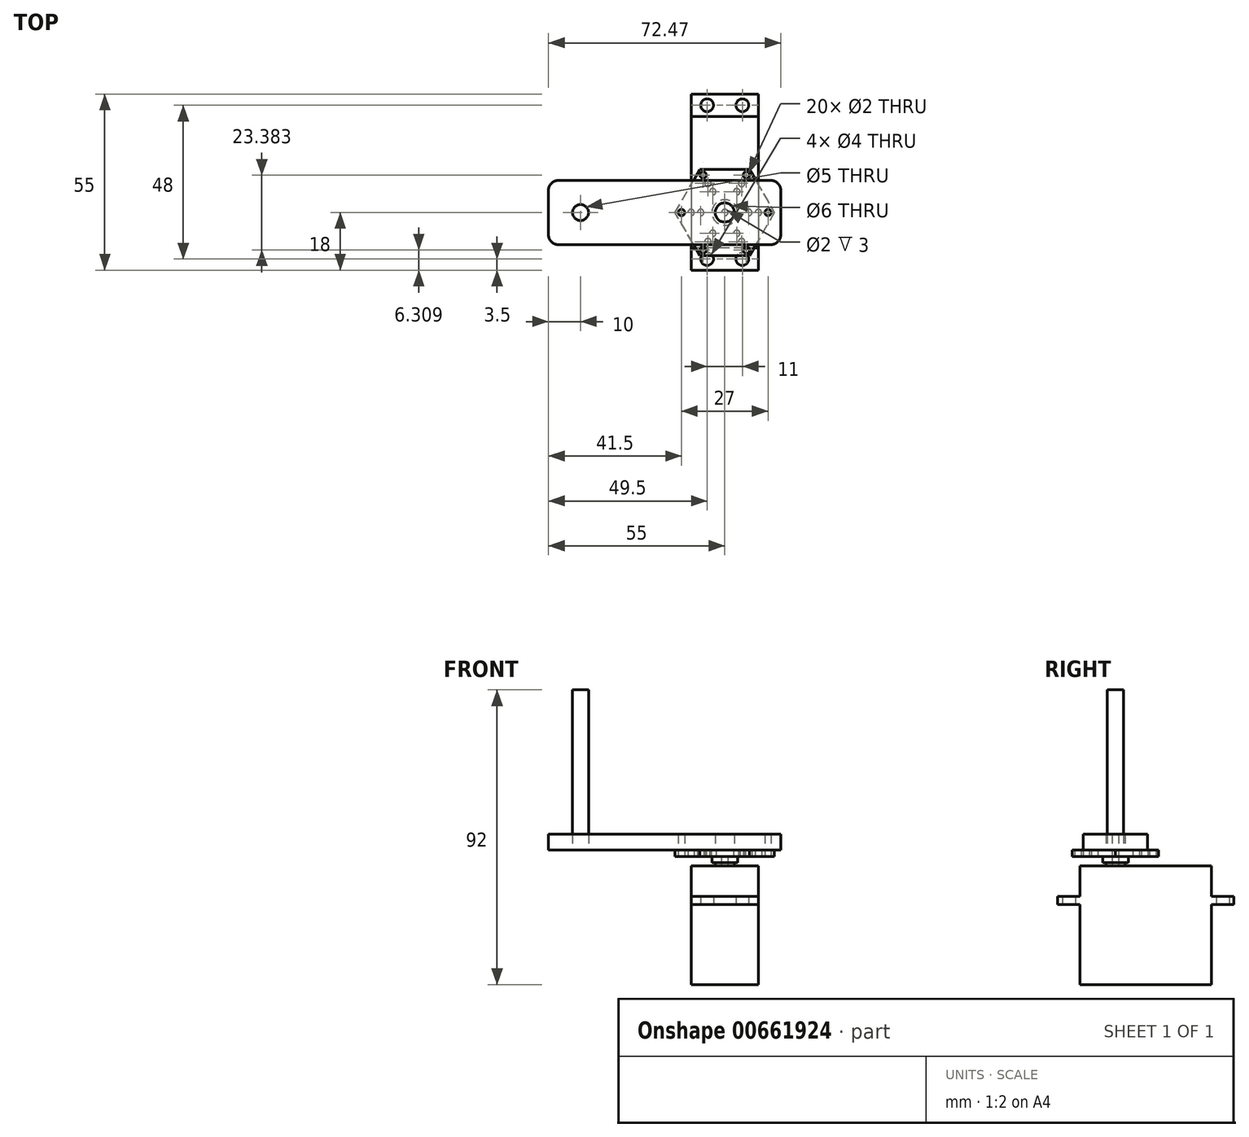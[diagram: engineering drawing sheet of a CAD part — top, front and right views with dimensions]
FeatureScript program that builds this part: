
annotation { "Feature Type Name" : "Feature", "Feature Type Description" : "" }
export const myFeature = defineFeature(function(context is Context, id is Id, definition is map)
    precondition{}
    {
        {
            var Q0;
            Q0=qCreatedBy(makeId("Top.planeOp"),FACE);
            var sketch = newSketch(context, id + "F0", { "sketchPlane" : qUnion([Q0])});
            skLineSegment(sketch, "E0.bottom", {"start": v(10.5, 20.5) * mm, "end": v(-10.5, 20.5) * mm});
            skLineSegment(sketch, "E0.top", {"start": v(10.5, -20.5) * mm, "end": v(-10.5, -20.5) * mm});
            skLineSegment(sketch, "E0.left", {"start": v(10.5, 20.5) * mm, "end": v(10.5, -20.5) * mm});
            skLineSegment(sketch, "E0.right", {"start": v(-10.5, 20.5) * mm, "end": v(-10.5, -20.5) * mm});
            skPoint(sketch, "E0.middle", {"position": v(0, 0) * mm});
            skSolve(sketch);
        }
        {
            var Q0;
            Q0 = qSketchRegion(id + "F0", true);
            extrude(context, id + "F1", {"entities" : qUnion([Q0]), "depth" : 12 * mm, "offsetDistance" : 25 * mm, "hasSecondDirection" : true, "secondDirectionOppositeDirection" : true, "secondDirectionDepth" : 25 * mm});
        }
        {
            var Q0;
            Q0=qCreatedBy(makeId("Top.planeOp"),FACE);
            var sketch = newSketch(context, id + "F2", { "sketchPlane" : qUnion([Q0])});
            skLineSegment(sketch, "E1.bottom", {"start": v(10.5, 27.5) * mm, "end": v(-10.5, 27.5) * mm});
            skLineSegment(sketch, "E1.top", {"start": v(10.5, -27.5) * mm, "end": v(-10.5, -27.5) * mm});
            skLineSegment(sketch, "E1.left", {"start": v(10.5, 27.5) * mm, "end": v(10.5, -27.5) * mm});
            skLineSegment(sketch, "E1.right", {"start": v(-10.5, 27.5) * mm, "end": v(-10.5, -27.5) * mm});
            skPoint(sketch, "E1.middle", {"position": v(0, 0) * mm});
            skLineSegment(sketch, "E2", {"start": v(0, 32.48) * mm, "end": v(0, -40.95) * mm, "construction": true});
            skPoint(sketch, "E2.endSnap0", {"position": v(0, -27.5) * mm});
            skCircle(sketch, "E3", {"center": v(-5.5, 24) * mm, "radius": 2 * mm});
            skLineSegment(sketch, "E4", {"start": v(-14.54, 0) * mm, "end": v(15.38, 0) * mm, "construction": true});
            skCircle(sketch, "E5.MirrorC", {"center": v(5.5, 24) * mm, "radius": 2 * mm});
            skCircle(sketch, "E6.MirrorC", {"center": v(5.5, -24) * mm, "radius": 2 * mm});
            skCircle(sketch, "E7.MirrorC", {"center": v(-5.5, -24) * mm, "radius": 2 * mm});
            skSolve(sketch);
        }
        {
            var Q0;
            Q0 = qSketchRegion(id + "F2", true);
            extrude(context, id + "F3", {"entities" : qUnion([Q0]), "operationType" : NewBodyOperationType.ADD, "depth" : 2.5 * mm, "offsetDistance" : 25 * mm});
        }
        {
            var Q0;
            Q0=makeQuery(id+"F1.opExtrude","CAP_FACE",FACE,{"disambiguationData":[OSD([sQuery(id+"F0.wireOp",EDGE,"E0.bottom"),sQuery(id+"F0.wireOp",EDGE,"E0.top"),sQuery(id+"F0.wireOp",EDGE,"E0.left"),sQuery(id+"F0.wireOp",EDGE,"E0.right")])],"isStart":false});
            var sketch = newSketch(context, id + "F4", { "sketchPlane" : qUnion([Q0])});
            skCircle(sketch, "E8", {"center": v(0, -9.5) * mm, "radius": 3 * mm});
            skCircle(sketch, "E9", {"center": v(0, -9.5) * mm, "radius": 1 * mm});
            skSolve(sketch);
        }
        {
            var Q0;
            Q0 = qSketchRegion(id + "F4", true);
            extrude(context, id + "F5", {"entities" : qUnion([Q0]), "operationType" : NewBodyOperationType.ADD, "depth" : 3 * mm, "offsetDistance" : 25 * mm});
        }
        {
            var Q0;
            Q0=makeQuery(id+"F5.opExtrude","CAP_FACE",FACE,{"disambiguationData":[OSD([sQuery(id+"F4.wireOp",EDGE,"E8"),sQuery(id+"F4.wireOp",EDGE,"E9")])],"isStart":false});
            var sketch = newSketch(context, id + "F6", { "sketchPlane" : qUnion([Q0])});
            skCircle(sketch, "E10", {"center": v(0, -9.5) * mm, "radius": 3 * mm});
            skCircle(sketch, "E11", {"center": v(0, -9.5) * mm, "radius": 4 * mm});
            skSolve(sketch);
        }
        {
            var Q0;
            Q0 = qSketchRegion(id + "F6", true);
            extrude(context, id + "F7", {"entities" : qUnion([Q0]), "oppositeDirection" : true, "depth" : 2 * mm, "offsetDistance" : 25 * mm});
        }
        {
            var Q0;
            Q0=makeQuery(id+"F5.opExtrude","CAP_FACE",FACE,{"disambiguationData":[OSD([sQuery(id+"F4.wireOp",EDGE,"E8"),sQuery(id+"F4.wireOp",EDGE,"E9")])],"isStart":false});
            var sketch = newSketch(context, id + "F8", { "sketchPlane" : qUnion([Q0])});
            skCircle(sketch, "E12.cCircle", {"center": v(0, -9.5) * mm, "radius": 13.42 * mm, "construction": true});
            skLineSegment(sketch, "E12.0", {"start": v(7.75, 3.92) * mm, "end": v(15.5, -9.5) * mm});
            skLineSegment(sketch, "E12.1", {"start": v(15.5, -9.5) * mm, "end": v(7.75, -22.92) * mm});
            skLineSegment(sketch, "E12.2", {"start": v(7.75, -22.92) * mm, "end": v(-7.75, -22.92) * mm});
            skLineSegment(sketch, "E12.3", {"start": v(-7.75, -22.92) * mm, "end": v(-15.5, -9.5) * mm});
            skLineSegment(sketch, "E12.4", {"start": v(-15.5, -9.5) * mm, "end": v(-7.75, 3.92) * mm});
            skLineSegment(sketch, "E12.5", {"start": v(-7.75, 3.92) * mm, "end": v(7.75, 3.92) * mm});
            skPoint(sketch, "E12.0.midPoint", {"position": v(11.63, -2.79) * mm});
            skLineSegment(sketch, "E13", {"start": v(-7.75, 3.92) * mm, "end": v(0, -9.5) * mm, "construction": true});
            skCircle(sketch, "E14", {"center": v(-3.75, -3) * mm, "radius": 1 * mm});
            skCircle(sketch, "E15", {"center": v(-5.25, -0.4) * mm, "radius": 1 * mm});
            skCircle(sketch, "E16", {"center": v(-6.75, 2.2) * mm, "radius": 1 * mm});
            skCircle(sketch, "E17.1.0", {"center": v(-13.5, -9.5) * mm, "radius": 1 * mm});
            skCircle(sketch, "E17.1.1", {"center": v(-10.5, -9.5) * mm, "radius": 1 * mm});
            skCircle(sketch, "E17.1.2", {"center": v(-7.5, -9.5) * mm, "radius": 1 * mm});
            skCircle(sketch, "E17.2.0", {"center": v(-6.75, -21.2) * mm, "radius": 1 * mm});
            skCircle(sketch, "E17.2.1", {"center": v(-5.25, -18.6) * mm, "radius": 1 * mm});
            skCircle(sketch, "E17.2.2", {"center": v(-3.75, -16) * mm, "radius": 1 * mm});
            skCircle(sketch, "E17.3.0", {"center": v(6.75, -21.2) * mm, "radius": 1 * mm});
            skCircle(sketch, "E17.3.1", {"center": v(5.25, -18.6) * mm, "radius": 1 * mm});
            skCircle(sketch, "E17.3.2", {"center": v(3.75, -16) * mm, "radius": 1 * mm});
            skCircle(sketch, "E17.4.0", {"center": v(13.5, -9.5) * mm, "radius": 1 * mm});
            skCircle(sketch, "E17.4.1", {"center": v(10.5, -9.5) * mm, "radius": 1 * mm});
            skCircle(sketch, "E17.4.2", {"center": v(7.5, -9.5) * mm, "radius": 1 * mm});
            skCircle(sketch, "E17.5.0", {"center": v(6.75, 2.2) * mm, "radius": 1 * mm});
            skCircle(sketch, "E17.5.1", {"center": v(5.25, -0.4) * mm, "radius": 1 * mm});
            skCircle(sketch, "E17.5.2", {"center": v(3.75, -3) * mm, "radius": 1 * mm});
            skSolve(sketch);
        }
        {
            var Q0;
            Q0 = qSketchRegion(id + "F8", true);
            extrude(context, id + "F9", {"entities" : qUnion([Q0]), "operationType" : NewBodyOperationType.ADD, "depth" : 2 * mm, "offsetDistance" : 25 * mm});
        }
        {
            var Q0;
            Q0=makeQuery(id+"F9.opExtrude","CAP_FACE",FACE,{"disambiguationData":[OSD([sQuery(id+"F8.wireOp",EDGE,"E12.0"),sQuery(id+"F8.wireOp",EDGE,"E12.1"),sQuery(id+"F8.wireOp",EDGE,"E12.2"),sQuery(id+"F8.wireOp",EDGE,"E12.3"),sQuery(id+"F8.wireOp",EDGE,"E12.4"),sQuery(id+"F8.wireOp",EDGE,"E12.5"),sQuery(id+"F8.wireOp",EDGE,"E14"),sQuery(id+"F8.wireOp",EDGE,"E15"),sQuery(id+"F8.wireOp",EDGE,"E16"),sQuery(id+"F8.wireOp",EDGE,"E17.1.0"),sQuery(id+"F8.wireOp",EDGE,"E17.1.1"),sQuery(id+"F8.wireOp",EDGE,"E17.1.2"),sQuery(id+"F8.wireOp",EDGE,"E17.2.0"),sQuery(id+"F8.wireOp",EDGE,"E17.2.1"),sQuery(id+"F8.wireOp",EDGE,"E17.2.2"),sQuery(id+"F8.wireOp",EDGE,"E17.3.0"),sQuery(id+"F8.wireOp",EDGE,"E17.3.1"),sQuery(id+"F8.wireOp",EDGE,"E17.3.2"),sQuery(id+"F8.wireOp",EDGE,"E17.4.0"),sQuery(id+"F8.wireOp",EDGE,"E17.4.1"),sQuery(id+"F8.wireOp",EDGE,"E17.4.2"),sQuery(id+"F8.wireOp",EDGE,"E17.5.0"),sQuery(id+"F8.wireOp",EDGE,"E17.5.1"),sQuery(id+"F8.wireOp",EDGE,"E17.5.2")])],"isStart":false});
            var sketch = newSketch(context, id + "F10", { "sketchPlane" : qUnion([Q0])});
            skLineSegment(sketch, "E18", {"start": v(-13.5, -9.5) * mm, "end": v(13.5, -9.5) * mm, "construction": true});
            skPoint(sketch, "E19", {"position": v(0, -9.5) * mm});
            skLineSegment(sketch, "E20.bottom", {"start": v(14.47, 0.5) * mm, "end": v(-52, 0.5) * mm});
            skLineSegment(sketch, "E20.top", {"start": v(14.47, -19.5) * mm, "end": v(-52, -19.5) * mm});
            skLineSegment(sketch, "E20.left", {"start": v(17.47, -2.5) * mm, "end": v(17.47, -16.5) * mm});
            skLineSegment(sketch, "E20.right", {"start": v(-55, -2.5) * mm, "end": v(-55, -16.5) * mm});
            skPoint(sketch, "E21", {"position": v(17.47, -9.5) * mm});
            skLineSegment(sketch, "E22", {"start": v(13.5, -9.5) * mm, "end": v(17.47, -9.5) * mm, "construction": true});
            skCircle(sketch, "E23", {"center": v(-13.5, -9.5) * mm, "radius": 1 * mm});
            skCircle(sketch, "E24", {"center": v(13.5, -9.5) * mm, "radius": 1 * mm});
            skCircle(sketch, "E25", {"center": v(-45, -9.5) * mm, "radius": 2.5 * mm});
            skPoint(sketch, "E26.visualSharp", {"position": v(-55, 0.5) * mm});
            skArc(sketch, "E26.filletArc", {"start": v(-52, 0.5) * mm, "mid": v(-54.12, -0.38) * mm, "end": v(-55, -2.5) * mm});
            skPoint(sketch, "E27.visualSharp", {"position": v(-55, -19.5) * mm});
            skArc(sketch, "E27.filletArc", {"start": v(-55, -16.5) * mm, "mid": v(-54.12, -18.62) * mm, "end": v(-52, -19.5) * mm});
            skPoint(sketch, "E28.visualSharp", {"position": v(17.47, -19.5) * mm});
            skArc(sketch, "E28.filletArc", {"start": v(14.47, -19.5) * mm, "mid": v(16.6, -18.62) * mm, "end": v(17.47, -16.5) * mm});
            skPoint(sketch, "E29.visualSharp", {"position": v(17.47, 0.5) * mm});
            skArc(sketch, "E29.filletArc", {"start": v(17.47, -2.5) * mm, "mid": v(16.6, -0.38) * mm, "end": v(14.47, 0.5) * mm});
            skCircle(sketch, "E30", {"center": v(0, -9.5) * mm, "radius": 3 * mm});
            skSolve(sketch);
        }
        {
            var Q0;
            Q0 = qSketchRegion(id + "F10", true);
            extrude(context, id + "F11", {"entities" : qUnion([Q0]), "depth" : 5 * mm, "offsetDistance" : 25 * mm});
        }
        {
            var Q0;
            Q0=makeQuery(id+"F11.opExtrude","CAP_FACE",FACE,{"disambiguationData":[OSD([sQuery(id+"F10.wireOp",EDGE,"E20.bottom"),sQuery(id+"F10.wireOp",EDGE,"E20.top"),sQuery(id+"F10.wireOp",EDGE,"E20.left"),sQuery(id+"F10.wireOp",EDGE,"E20.right"),sQuery(id+"F10.wireOp",EDGE,"E23"),sQuery(id+"F10.wireOp",EDGE,"E24"),sQuery(id+"F10.wireOp",EDGE,"E25"),sQuery(id+"F10.wireOp",EDGE,"E26.filletArc"),sQuery(id+"F10.wireOp",EDGE,"E27.filletArc"),sQuery(id+"F10.wireOp",EDGE,"E28.filletArc"),sQuery(id+"F10.wireOp",EDGE,"E29.filletArc"),sQuery(id+"F10.wireOp",EDGE,"E30")])],"isStart":true});
            var sketch = newSketch(context, id + "F12", { "sketchPlane" : qUnion([Q0])});
            skCircle(sketch, "E31", {"center": v(-45, 9.5) * mm, "radius": 2.5 * mm});
            skSolve(sketch);
        }
        {
            var Q0;
            Q0 = qSketchRegion(id + "F12", true);
            extrude(context, id + "F13", {"entities" : qUnion([Q0]), "oppositeDirection" : true, "depth" : 50 * mm, "offsetDistance" : 25 * mm});
        }
    });
